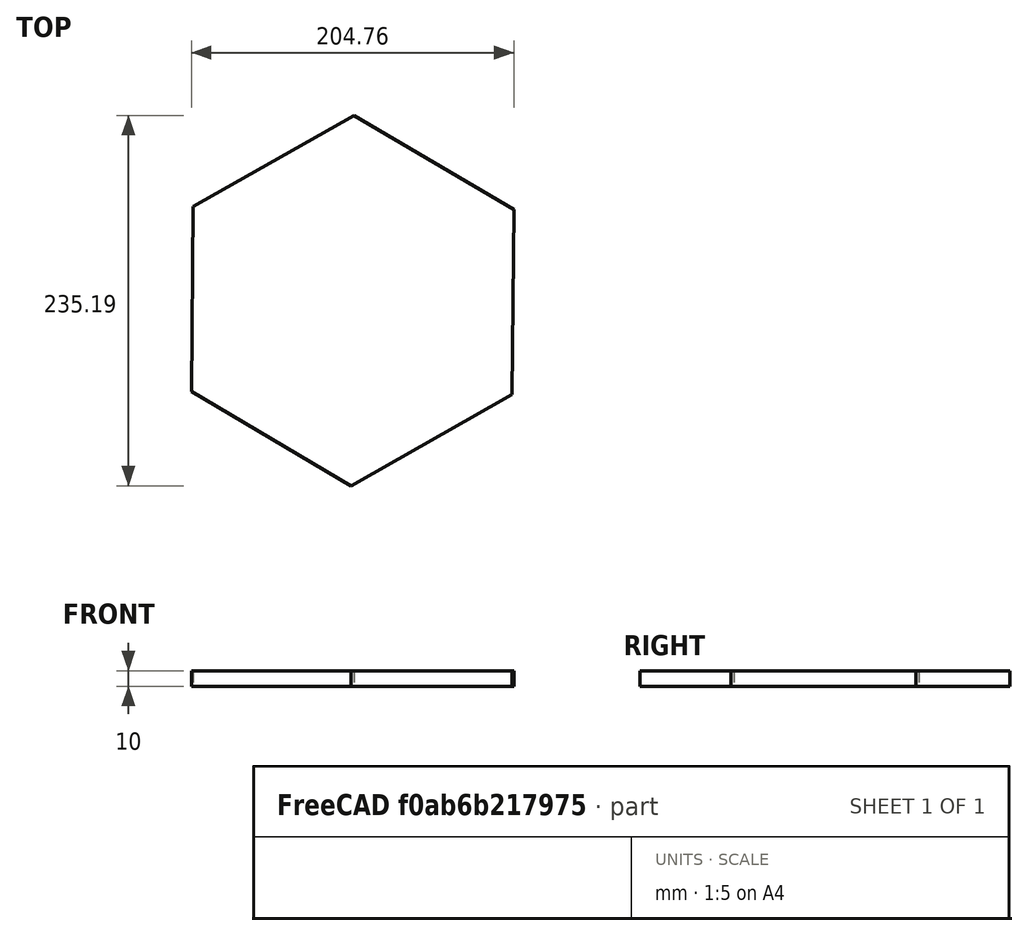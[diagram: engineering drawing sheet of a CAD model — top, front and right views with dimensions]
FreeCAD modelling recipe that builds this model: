
FCSTD DOCUMENT  (FreeCAD 0.19R)
Label: Board Hexagon
License: All rights reserved
LicenseURL: http://en.wikipedia.org/wiki/All_rights_reserved
objects: Sketcher::SketchObject×1, PartDesign::Pad×1, PartDesign::Body×1
note: 4 computed .brp shape members not serialized (recipe doc carries the construction recipe); baked Part::Feature solids carry a one-line shape summary decoded from their .brp

FEATURE [Sketcher::SketchObject] Sketch013  label="Board"
  FullyConstrained = false
  MapMode = 5
  Support = -> [XY_Plane013]
  sketch-geometry (7):
    g0: LineSegment StartX=40.648 StartY=7.96072 StartZ=0 EndX=-60.6547 EndY=67.6901 EndZ=0
    g1: LineSegment StartX=-60.6547 StartY=67.6901 StartZ=0 EndX=-163.033 EndY=9.82395 EndZ=0
    g2: LineSegment StartX=-163.033 StartY=9.82395 StartZ=0 EndX=-164.109 EndY=-107.771 EndZ=0
    g3: LineSegment StartX=-164.109 StartY=-107.771 StartZ=0 EndX=-62.8062 EndY=-167.501 EndZ=0
    g4: LineSegment StartX=-62.8062 StartY=-167.501 StartZ=0 EndX=39.5723 EndY=-109.635 EndZ=0
    g5: LineSegment StartX=39.5723 StartY=-109.635 StartZ=0 EndX=40.648 EndY=7.96072 EndZ=0
    g6: Circle CenterX=-61.7305 CenterY=-49.9054 CenterZ=0 NormalX=0 NormalY=0 NormalZ=1 AngleXU=0 Radius=117.6
  constraints (13):
    c: Coincident(g0,g1)
    c: Coincident(g1,g2)
    c: Coincident(g2,g3)
    c: Coincident(g3,g4)
    c: Coincident(g4,g5)
    c: Coincident(g5,g0)
    c: Equal(g0, g1-g5) x5
    c: PointOnObject(g0,g6)
    c: PointOnObject(g1,g6)
    c: PointOnObject(g2,g6)
    c: PointOnObject(g3,g6)
    c: PointOnObject(g4,g6)
    c: PointOnObject(g5,g6)
FEATURE [PartDesign::Pad] Pad013
  Direction = (1,1,1)
  Length = 10
  Length2 = 100
  Profile = -> Sketch013
  Reversed = true
  Type = 0
FEATURE [PartDesign::Body] Body013  label="Board Body"
  Group = -> [Sketch013,Pad013]
  Origin = -> Origin013
  Placement = pos=(164.109,167.501,0) rot=(0,0,1;0rad)
  Tip = -> Pad013
